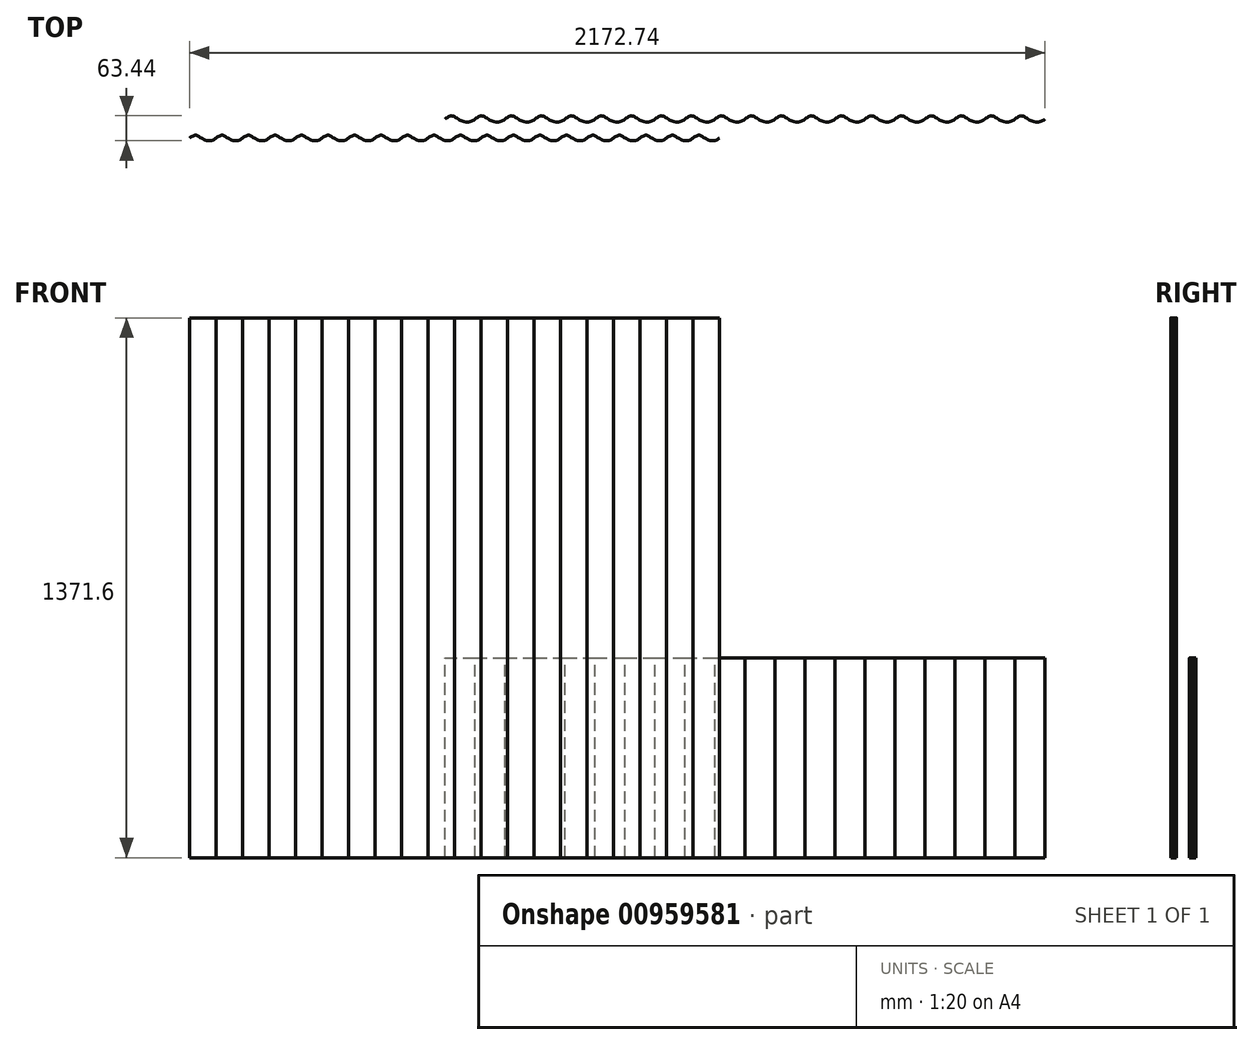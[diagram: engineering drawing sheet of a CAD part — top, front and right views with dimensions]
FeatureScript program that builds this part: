
annotation { "Feature Type Name" : "Feature", "Feature Type Description" : "" }
export const myFeature = defineFeature(function(context is Context, id is Id, definition is map)
    precondition{}
    {
        {
            var Q0;
            Q0=qCreatedBy(makeId("Top.planeOp"),FACE);
            var sketch = newSketch(context, id + "F0", { "sketchPlane" : qUnion([Q0])});
            skFitSpline(sketch, "E0", {"points": [v(-76.2, 0) * mm, v(-59.35, 8.43) * mm, v(-42.5, 0) * mm, v(-18.32, -7.7) * mm, v(0, 0) * mm], "startDerivative": vector(71.9, 53.55) * mm, "endDerivative": vector(70.3, 44.56) * mm});
            skFitSpline(sketch, "E1", {"points": [v(0, 0) * mm, v(16.85, 8.43) * mm, v(33.7, 0) * mm, v(57.88, -7.7) * mm, v(76.2, 0) * mm], "startDerivative": vector(71.9, 53.55) * mm, "endDerivative": vector(70.3, 44.56) * mm});
            skFitSpline(sketch, "E2", {"points": [v(76.2, 0) * mm, v(93.05, 8.43) * mm, v(109.9, 0) * mm, v(134.08, -7.7) * mm, v(152.4, 0) * mm], "startDerivative": vector(71.9, 53.55) * mm, "endDerivative": vector(70.3, 44.56) * mm});
            skFitSpline(sketch, "E3", {"points": [v(152.4, 0) * mm, v(169.25, 8.43) * mm, v(186.1, 0) * mm, v(210.28, -7.7) * mm, v(228.6, 0) * mm], "startDerivative": vector(71.9, 53.55) * mm, "endDerivative": vector(70.3, 44.56) * mm});
            skFitSpline(sketch, "E4", {"points": [v(228.6, 0) * mm, v(245.45, 8.43) * mm, v(262.3, 0) * mm, v(286.48, -7.7) * mm, v(304.8, 0) * mm], "startDerivative": vector(71.9, 53.55) * mm, "endDerivative": vector(70.3, 44.56) * mm});
            skFitSpline(sketch, "E5", {"points": [v(304.8, 0) * mm, v(321.65, 8.43) * mm, v(338.5, 0) * mm, v(362.68, -7.7) * mm, v(381, 0) * mm], "startDerivative": vector(71.9, 53.55) * mm, "endDerivative": vector(70.3, 44.56) * mm});
            skFitSpline(sketch, "E6", {"points": [v(381, 0) * mm, v(397.85, 8.43) * mm, v(414.7, 0) * mm, v(438.88, -7.7) * mm, v(457.2, 0) * mm], "startDerivative": vector(71.9, 53.55) * mm, "endDerivative": vector(70.3, 44.56) * mm});
            skFitSpline(sketch, "E7", {"points": [v(457.2, 0) * mm, v(474.05, 8.43) * mm, v(490.9, 0) * mm, v(515.08, -7.7) * mm, v(533.4, 0) * mm], "startDerivative": vector(71.9, 53.55) * mm, "endDerivative": vector(70.3, 44.56) * mm});
            skFitSpline(sketch, "E8", {"points": [v(533.4, 0) * mm, v(550.25, 8.43) * mm, v(567.1, 0) * mm, v(591.28, -7.7) * mm, v(609.6, 0) * mm], "startDerivative": vector(71.9, 53.55) * mm, "endDerivative": vector(70.3, 44.56) * mm});
            skFitSpline(sketch, "E9", {"points": [v(609.6, 0) * mm, v(626.45, 8.43) * mm, v(643.3, 0) * mm, v(667.48, -7.7) * mm, v(685.8, 0) * mm], "startDerivative": vector(71.9, 53.55) * mm, "endDerivative": vector(70.3, 44.56) * mm});
            skFitSpline(sketch, "E10", {"points": [v(685.8, 0) * mm, v(702.65, 8.43) * mm, v(719.5, 0) * mm, v(743.68, -7.7) * mm, v(762, 0) * mm], "startDerivative": vector(71.9, 53.55) * mm, "endDerivative": vector(70.3, 44.56) * mm});
            skFitSpline(sketch, "E11", {"points": [v(762, 0) * mm, v(778.85, 8.43) * mm, v(795.7, 0) * mm, v(819.88, -7.7) * mm, v(838.2, 0) * mm], "startDerivative": vector(71.9, 53.55) * mm, "endDerivative": vector(70.3, 44.56) * mm});
            skFitSpline(sketch, "E12", {"points": [v(838.2, 0) * mm, v(855.05, 8.43) * mm, v(871.9, 0) * mm, v(896.08, -7.7) * mm, v(914.4, 0) * mm], "startDerivative": vector(71.9, 53.55) * mm, "endDerivative": vector(70.3, 44.56) * mm});
            skFitSpline(sketch, "E13", {"points": [v(914.4, 0) * mm, v(931.25, 8.43) * mm, v(948.1, 0) * mm, v(972.28, -7.7) * mm, v(990.6, 0) * mm], "startDerivative": vector(71.9, 53.55) * mm, "endDerivative": vector(70.3, 44.56) * mm});
            skFitSpline(sketch, "E14", {"points": [v(990.6, 0) * mm, v(1007.45, 8.43) * mm, v(1024.3, 0) * mm, v(1048.48, -7.7) * mm, v(1066.8, 0) * mm], "startDerivative": vector(71.9, 53.55) * mm, "endDerivative": vector(70.3, 44.56) * mm});
            skFitSpline(sketch, "E15", {"points": [v(1066.8, 0) * mm, v(1083.65, 8.43) * mm, v(1100.5, 0) * mm, v(1124.68, -7.7) * mm, v(1143, 0) * mm], "startDerivative": vector(71.9, 53.55) * mm, "endDerivative": vector(70.3, 44.56) * mm});
            skFitSpline(sketch, "E16", {"points": [v(1143, 0) * mm, v(1159.85, 8.43) * mm, v(1176.7, 0) * mm, v(1200.88, -7.7) * mm, v(1219.2, 0) * mm], "startDerivative": vector(71.9, 53.55) * mm, "endDerivative": vector(70.3, 44.56) * mm});
            skFitSpline(sketch, "E17", {"points": [v(1219.2, 0) * mm, v(1236.05, 8.43) * mm, v(1252.9, 0) * mm, v(1277.08, -7.7) * mm, v(1295.4, 0) * mm], "startDerivative": vector(71.9, 53.55) * mm, "endDerivative": vector(70.3, 44.56) * mm});
            skFitSpline(sketch, "E18", {"points": [v(1295.4, 0) * mm, v(1312.25, 8.43) * mm, v(1329.1, 0) * mm, v(1353.28, -7.7) * mm, v(1371.6, 0) * mm], "startDerivative": vector(71.9, 53.55) * mm, "endDerivative": vector(70.3, 44.56) * mm});
            skFitSpline(sketch, "E19", {"points": [v(1371.6, 0) * mm, v(1388.45, 8.43) * mm, v(1405.3, 0) * mm, v(1429.48, -7.7) * mm, v(1447.8, 0) * mm], "startDerivative": vector(71.9, 53.55) * mm, "endDerivative": vector(70.3, 44.56) * mm});
            skSolve(sketch);
        }
        {
            var Q0;
            Q0=qCreatedBy(makeId("Top.planeOp"),FACE);
            var sketch = newSketch(context, id + "F1", { "sketchPlane" : qUnion([Q0])});
            skFitSpline(sketch, "E20", {"points": [v(-724.94, -48.18) * mm, v(-710.06, -40.73) * mm, v(-695.17, -48.18) * mm, v(-673.81, -54.97) * mm, v(-657.63, -48.18) * mm], "startDerivative": vector(63.5, 47.3) * mm, "endDerivative": vector(62.1, 39.37) * mm});
            skFitSpline(sketch, "E21", {"points": [v(-657.63, -48.18) * mm, v(-642.75, -40.73) * mm, v(-627.86, -48.18) * mm, v(-606.5, -54.97) * mm, v(-590.32, -48.18) * mm], "startDerivative": vector(63.5, 47.3) * mm, "endDerivative": vector(62.1, 39.37) * mm});
            skFitSpline(sketch, "E22", {"points": [v(-590.32, -48.18) * mm, v(-575.44, -40.73) * mm, v(-560.55, -48.18) * mm, v(-539.2, -54.97) * mm, v(-523.01, -48.18) * mm], "startDerivative": vector(63.5, 47.3) * mm, "endDerivative": vector(62.1, 39.37) * mm});
            skFitSpline(sketch, "E23", {"points": [v(-523.01, -48.18) * mm, v(-508.13, -40.73) * mm, v(-493.24, -48.18) * mm, v(-471.88, -54.97) * mm, v(-455.7, -48.18) * mm], "startDerivative": vector(63.5, 47.3) * mm, "endDerivative": vector(62.1, 39.37) * mm});
            skFitSpline(sketch, "E24", {"points": [v(-455.7, -48.18) * mm, v(-440.82, -40.73) * mm, v(-425.93, -48.18) * mm, v(-404.57, -54.97) * mm, v(-388.4, -48.18) * mm], "startDerivative": vector(63.5, 47.3) * mm, "endDerivative": vector(62.1, 39.37) * mm});
            skFitSpline(sketch, "E25", {"points": [v(-388.4, -48.18) * mm, v(-373.5, -40.73) * mm, v(-358.62, -48.18) * mm, v(-337.26, -54.97) * mm, v(-321.08, -48.18) * mm], "startDerivative": vector(63.5, 47.3) * mm, "endDerivative": vector(62.1, 39.37) * mm});
            skFitSpline(sketch, "E26", {"points": [v(-321.08, -48.18) * mm, v(-306.2, -40.73) * mm, v(-291.3, -48.18) * mm, v(-269.95, -54.97) * mm, v(-253.77, -48.18) * mm], "startDerivative": vector(63.5, 47.3) * mm, "endDerivative": vector(62.1, 39.37) * mm});
            skFitSpline(sketch, "E27", {"points": [v(-253.77, -48.18) * mm, v(-238.89, -40.73) * mm, v(-224, -48.18) * mm, v(-202.64, -54.97) * mm, v(-186.46, -48.18) * mm], "startDerivative": vector(63.5, 47.3) * mm, "endDerivative": vector(62.1, 39.37) * mm});
            skFitSpline(sketch, "E28", {"points": [v(-186.46, -48.18) * mm, v(-171.58, -40.73) * mm, v(-156.69, -48.18) * mm, v(-135.33, -54.97) * mm, v(-119.15, -48.18) * mm], "startDerivative": vector(63.5, 47.3) * mm, "endDerivative": vector(62.1, 39.37) * mm});
            skFitSpline(sketch, "E29", {"points": [v(-119.15, -48.18) * mm, v(-104.27, -40.73) * mm, v(-89.38, -48.18) * mm, v(-68.02, -54.97) * mm, v(-51.84, -48.18) * mm], "startDerivative": vector(63.5, 47.3) * mm, "endDerivative": vector(62.1, 39.37) * mm});
            skFitSpline(sketch, "E30", {"points": [v(-51.84, -48.18) * mm, v(-36.96, -40.73) * mm, v(-22.07, -48.18) * mm, v(-0.71, -54.97) * mm, v(15.47, -48.18) * mm], "startDerivative": vector(63.5, 47.3) * mm, "endDerivative": vector(62.1, 39.37) * mm});
            skFitSpline(sketch, "E31", {"points": [v(15.47, -48.18) * mm, v(30.35, -40.73) * mm, v(45.24, -48.18) * mm, v(66.6, -54.97) * mm, v(82.78, -48.18) * mm], "startDerivative": vector(63.5, 47.3) * mm, "endDerivative": vector(62.1, 39.37) * mm});
            skFitSpline(sketch, "E32", {"points": [v(82.78, -48.18) * mm, v(97.66, -40.73) * mm, v(112.55, -48.18) * mm, v(133.9, -54.97) * mm, v(150.09, -48.18) * mm], "startDerivative": vector(63.5, 47.3) * mm, "endDerivative": vector(62.1, 39.37) * mm});
            skFitSpline(sketch, "E33", {"points": [v(150.09, -48.18) * mm, v(164.97, -40.73) * mm, v(179.86, -48.18) * mm, v(201.22, -54.97) * mm, v(217.4, -48.18) * mm], "startDerivative": vector(63.5, 47.3) * mm, "endDerivative": vector(62.1, 39.37) * mm});
            skFitSpline(sketch, "E34", {"points": [v(217.4, -48.18) * mm, v(232.28, -40.73) * mm, v(247.17, -48.18) * mm, v(268.53, -54.97) * mm, v(284.7, -48.18) * mm], "startDerivative": vector(63.5, 47.3) * mm, "endDerivative": vector(62.1, 39.37) * mm});
            skFitSpline(sketch, "E35", {"points": [v(284.7, -48.18) * mm, v(299.6, -40.73) * mm, v(314.48, -48.18) * mm, v(335.84, -54.97) * mm, v(352.02, -48.18) * mm], "startDerivative": vector(63.5, 47.3) * mm, "endDerivative": vector(62.1, 39.37) * mm});
            skFitSpline(sketch, "E36", {"points": [v(352.02, -48.18) * mm, v(366.9, -40.73) * mm, v(381.8, -48.18) * mm, v(403.15, -54.97) * mm, v(419.33, -48.18) * mm], "startDerivative": vector(63.5, 47.3) * mm, "endDerivative": vector(62.1, 39.37) * mm});
            skFitSpline(sketch, "E37", {"points": [v(419.33, -48.18) * mm, v(434.21, -40.73) * mm, v(449.1, -48.18) * mm, v(470.46, -54.97) * mm, v(486.64, -48.18) * mm], "startDerivative": vector(63.5, 47.3) * mm, "endDerivative": vector(62.1, 39.37) * mm});
            skFitSpline(sketch, "E38", {"points": [v(486.64, -48.18) * mm, v(501.52, -40.73) * mm, v(516.41, -48.18) * mm, v(537.77, -54.97) * mm, v(553.95, -48.18) * mm], "startDerivative": vector(63.5, 47.3) * mm, "endDerivative": vector(62.1, 39.37) * mm});
            skFitSpline(sketch, "E39", {"points": [v(553.95, -48.18) * mm, v(568.83, -40.73) * mm, v(583.72, -48.18) * mm, v(605.08, -54.97) * mm, v(621.26, -48.18) * mm], "startDerivative": vector(63.5, 47.3) * mm, "endDerivative": vector(62.1, 39.37) * mm});
            skSolve(sketch);
        }
        {
            var Q0;
            Q0=qSketchRegion(id+"F0",true);
            var Q1;
            Q1=qConstructionFilter(qBodyType(qCreatedBy(id+"F0",EDGE),BodyType.WIRE),ConstructionObject.NO);
            extrude(context, id + "F2", {"entities" : qUnion([Q0]), "bodyType" : ToolBodyType.SURFACE, "operationType" : NewBodyOperationType.ADD, "surfaceEntities" : qUnion([Q1]), "depth" : 508 * mm, "offsetDistance" : 25.4 * mm});
        }
        {
            var Q0;
            Q0=qSketchRegion(id+"F1",true);
            var Q1;
            Q1=qConstructionFilter(qBodyType(qCreatedBy(id+"F1",EDGE),BodyType.WIRE),ConstructionObject.NO);
            extrude(context, id + "F3", {"entities" : qUnion([Q0]), "bodyType" : ToolBodyType.SURFACE, "surfaceEntities" : qUnion([Q1]), "depth" : 1371.6 * mm, "offsetDistance" : 25.4 * mm});
        }
    });
